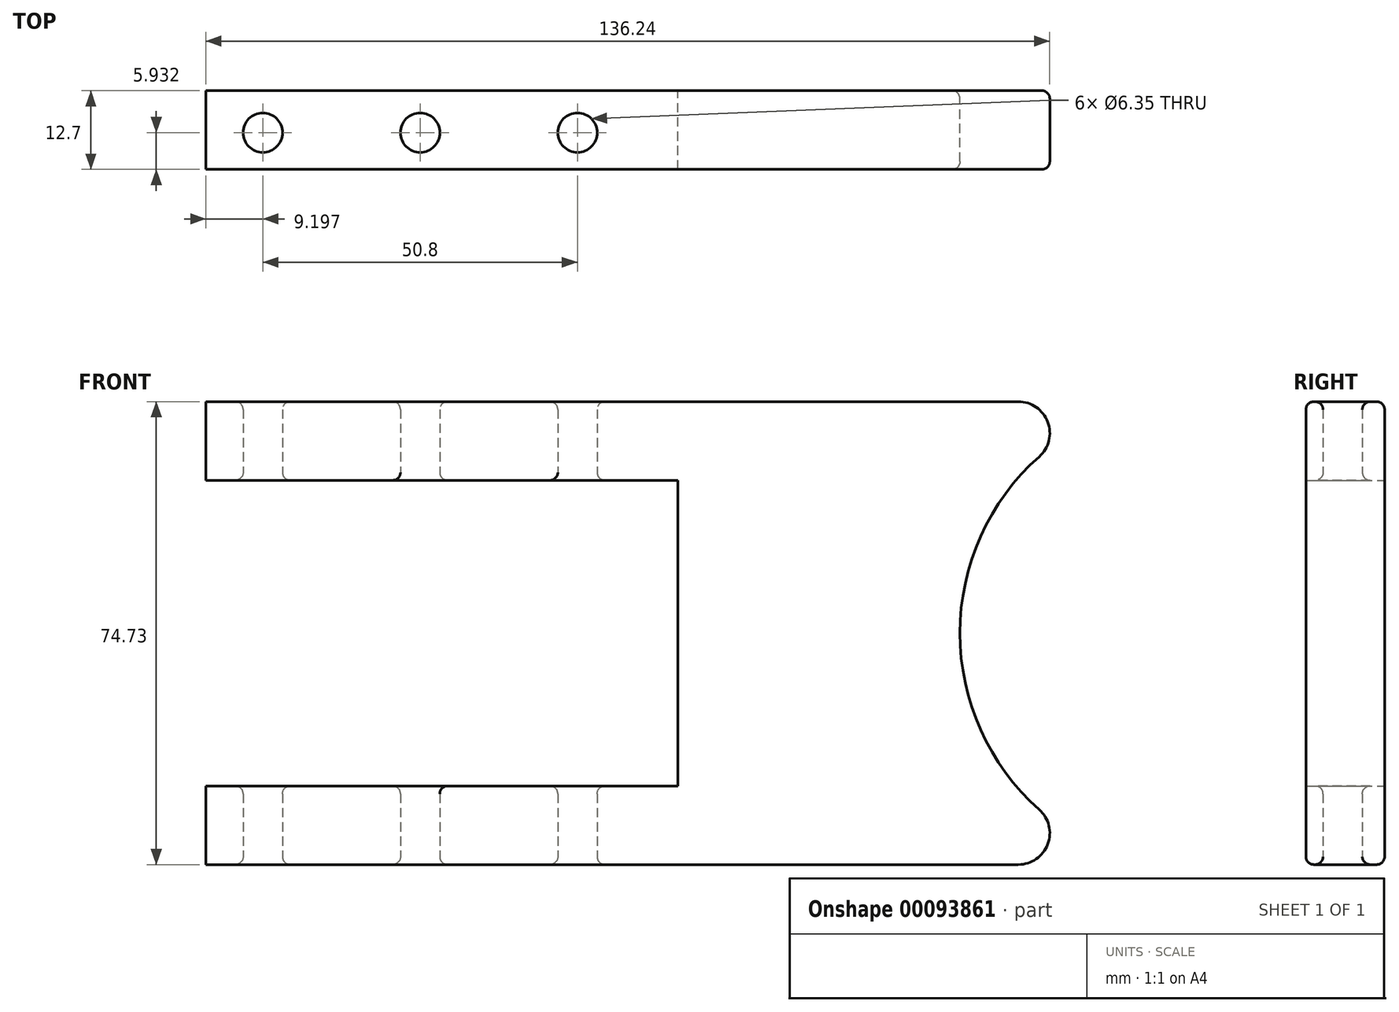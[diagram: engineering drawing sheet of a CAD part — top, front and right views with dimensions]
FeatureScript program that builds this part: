
annotation { "Feature Type Name" : "Feature", "Feature Type Description" : "" }
export const myFeature = defineFeature(function(context is Context, id is Id, definition is map)
    precondition{}
    {
        {
            var Q0;
            Q0=qCreatedBy(makeId("Front.planeOp"),FACE);
            var sketch = newSketch(context, id + "F0", { "sketchPlane" : qUnion([Q0])});
            skLineSegment(sketch, "E0.bottom", {"start": v(-76.46, 29.1) * mm, "end": v(75.94, 29.1) * mm});
            skLineSegment(sketch, "E0.top", {"start": v(-76.46, -45.63) * mm, "end": v(75.94, -45.63) * mm});
            skLineSegment(sketch, "E0.left", {"start": v(-76.46, 29.1) * mm, "end": v(-76.46, 16.4) * mm});
            skLineSegment(sketch, "E1", {"start": v(-76.46, 16.4) * mm, "end": v(-0.26, 16.4) * mm});
            skLineSegment(sketch, "E2", {"start": v(-0.26, 16.4) * mm, "end": v(-0.26, -32.93) * mm});
            skLineSegment(sketch, "E3", {"start": v(-0.26, -32.93) * mm, "end": v(-76.46, -32.93) * mm});
            skLineSegment(sketch, "E4.trimOffspring", {"start": v(-76.46, -32.93) * mm, "end": v(-76.46, -45.63) * mm});
            skArc(sketch, "E5", {"start": v(75.94, 29.1) * mm, "mid": v(45.28, -8.26) * mm, "end": v(75.94, -45.63) * mm});
            skSolve(sketch);
        }
        {
            var Q0;
            Q0=makeQuery(id+"F0.imprint","IMPRINT",FACE,{"disambiguationData":[TD([[makeQuery(id+"F0.imprint","IMPRINT",EDGE,{"derivedFrom":sQuery(id+"F0.wireOp",EDGE,"E0.bottom")}),-1.0]])]});
            extrude(context, id + "F1", {"entities" : qUnion([Q0]), "depth" : 12.7 * mm});
        }
        {
            var Q0;
            Q0=makeQuery(id+"F1.opExtrude","CAP_EDGE",EDGE,{"disambiguationData":[OSD([sQuery(id+"F0.wireOp",EDGE,"E0.bottom")])],"isStart":true});
            var Q1;
            Q1=makeQuery(id+"F1.opExtrude","CAP_EDGE",EDGE,{"disambiguationData":[OSD([sQuery(id+"F0.wireOp",EDGE,"E0.bottom")])],"isStart":false});
            var Q2;
            Q2=makeQuery(id+"F1.opExtrude","CAP_EDGE",EDGE,{"disambiguationData":[OSD([sQuery(id+"F0.wireOp",EDGE,"E5")])],"isStart":false});
            var Q3;
            Q3=makeQuery(id+"F1.opExtrude","CAP_EDGE",EDGE,{"disambiguationData":[OSD([sQuery(id+"F0.wireOp",EDGE,"E5")])],"isStart":true});
            var Q4;
            Q4=makeQuery(id+"F1.opExtrude","CAP_EDGE",EDGE,{"disambiguationData":[OSD([sQuery(id+"F0.wireOp",EDGE,"E0.top")])],"isStart":false});
            var Q5;
            Q5=makeQuery(id+"F1.opExtrude","CAP_EDGE",EDGE,{"disambiguationData":[OSD([sQuery(id+"F0.wireOp",EDGE,"E0.top")])],"isStart":true});
            fillet(context, id + "F2", {"entities" : qUnion([Q0, Q1, Q2, Q3, Q4, Q5]), "radius" : 1.27 * mm, "tangentPropagation" : true, "allowEdgeOverflow" : false});
        }
        {
            var Q0;
            Q0=qCreatedBy(makeId("Top.planeOp"),FACE);
            var sketch = newSketch(context, id + "F3", { "sketchPlane" : qUnion([Q0])});
            skCircle(sketch, "E6", {"center": v(-67.26, -6.77) * mm, "radius": 3.18 * mm});
            skCircle(sketch, "E7", {"center": v(-41.86, -6.77) * mm, "radius": 3.18 * mm});
            skCircle(sketch, "E8", {"center": v(-16.46, -6.77) * mm, "radius": 3.18 * mm});
            skSolve(sketch);
        }
        {
            var Q0;
            Q0=makeQuery(id+"F1.opExtrude","SWEPT_EDGE",EDGE,{"disambiguationData":[OSD([sQuery(id+"F0.wireOp",EDGE,"E0.bottom"),sQuery(id+"F0.wireOp",EDGE,"E5")])]});
            var Q1;
            Q1=makeQuery(id+"F1.opExtrude","SWEPT_EDGE",EDGE,{"disambiguationData":[OSD([sQuery(id+"F0.wireOp",EDGE,"E0.top"),sQuery(id+"F0.wireOp",EDGE,"E5")])]});
            fillet(context, id + "F4", {"entities" : qUnion([Q0, Q1]), "radius" : 5.08 * mm, "tangentPropagation" : true, "allowEdgeOverflow" : false});
        }
        {
            var Q0;
            Q0=makeQuery(id+"F3.imprint","IMPRINT",FACE,{"disambiguationData":[TD([[makeQuery(id+"F3.imprint","IMPRINT",EDGE,{"derivedFrom":sQuery(id+"F3.wireOp",EDGE,"E7")}),1.0]])]});
            var Q1;
            Q1=makeQuery(id+"F3.imprint","IMPRINT",FACE,{"disambiguationData":[TD([[makeQuery(id+"F3.imprint","IMPRINT",EDGE,{"derivedFrom":sQuery(id+"F3.wireOp",EDGE,"E8")}),1.0]])]});
            var Q2;
            Q2=makeQuery(id+"F3.imprint","IMPRINT",FACE,{"disambiguationData":[TD([[makeQuery(id+"F3.imprint","IMPRINT",EDGE,{"derivedFrom":sQuery(id+"F3.wireOp",EDGE,"E6")}),1.0]])]});
            var Q3;
            Q3=sQuery(id+"F3.wireOp",EDGE,"E8");
            var Q4;
            Q4=sQuery(id+"F3.wireOp",EDGE,"E7");
            var Q5;
            Q5=sQuery(id+"F3.wireOp",EDGE,"E6");
            extrude(context, id + "F5", {"entities" : qUnion([Q0, Q1, Q2]), "operationType" : NewBodyOperationType.REMOVE, "surfaceEntities" : qUnion([Q3, Q4, Q5]), "endBound" : BoundingType.SYMMETRIC, "depth" : 101.6 * mm});
        }
        {
            var Q0;
            Q0=makeQuery(id+"F5.boolean.opBoolean","INTERSECT",EDGE,{"derivedFrom":[makeQuery(id+"F1.opExtrude","SWEPT_FACE",FACE,{"disambiguationData":[OSD([sQuery(id+"F0.wireOp",EDGE,"E0.top")])]}),makeQuery(id+"F5.opExtrude","SWEPT_FACE",FACE,{"disambiguationData":[OSD([sQuery(id+"F3.wireOp",EDGE,"E7")])]})]});
            var Q1;
            Q1=makeQuery(id+"F5.boolean.opBoolean","INTERSECT",EDGE,{"derivedFrom":[makeQuery(id+"F1.opExtrude","SWEPT_FACE",FACE,{"disambiguationData":[OSD([sQuery(id+"F0.wireOp",EDGE,"E1")])]}),makeQuery(id+"F5.opExtrude","SWEPT_FACE",FACE,{"disambiguationData":[OSD([sQuery(id+"F3.wireOp",EDGE,"E7")])]})]});
            var Q2;
            Q2=makeQuery(id+"F5.boolean.opBoolean","INTERSECT",EDGE,{"derivedFrom":[makeQuery(id+"F1.opExtrude","SWEPT_FACE",FACE,{"disambiguationData":[OSD([sQuery(id+"F0.wireOp",EDGE,"E3")])]}),makeQuery(id+"F5.opExtrude","SWEPT_FACE",FACE,{"disambiguationData":[OSD([sQuery(id+"F3.wireOp",EDGE,"E7")])]})]});
            var Q3;
            Q3=makeQuery(id+"F5.boolean.opBoolean","INTERSECT",EDGE,{"derivedFrom":[makeQuery(id+"F1.opExtrude","SWEPT_FACE",FACE,{"disambiguationData":[OSD([sQuery(id+"F0.wireOp",EDGE,"E0.bottom")])]}),makeQuery(id+"F5.opExtrude","SWEPT_FACE",FACE,{"disambiguationData":[OSD([sQuery(id+"F3.wireOp",EDGE,"E7")])]})]});
            var Q4;
            Q4=makeQuery(id+"F5.boolean.opBoolean","INTERSECT",EDGE,{"derivedFrom":[makeQuery(id+"F1.opExtrude","SWEPT_FACE",FACE,{"disambiguationData":[OSD([sQuery(id+"F0.wireOp",EDGE,"E0.bottom")])]}),makeQuery(id+"F5.opExtrude","SWEPT_FACE",FACE,{"disambiguationData":[OSD([sQuery(id+"F3.wireOp",EDGE,"E8")])]})]});
            var Q5;
            Q5=makeQuery(id+"F5.boolean.opBoolean","INTERSECT",EDGE,{"derivedFrom":[makeQuery(id+"F1.opExtrude","SWEPT_FACE",FACE,{"disambiguationData":[OSD([sQuery(id+"F0.wireOp",EDGE,"E0.bottom")])]}),makeQuery(id+"F5.opExtrude","SWEPT_FACE",FACE,{"disambiguationData":[OSD([sQuery(id+"F3.wireOp",EDGE,"E6")])]})]});
            var Q6;
            Q6=makeQuery(id+"F5.boolean.opBoolean","INTERSECT",EDGE,{"derivedFrom":[makeQuery(id+"F1.opExtrude","SWEPT_FACE",FACE,{"disambiguationData":[OSD([sQuery(id+"F0.wireOp",EDGE,"E3")])]}),makeQuery(id+"F5.opExtrude","SWEPT_FACE",FACE,{"disambiguationData":[OSD([sQuery(id+"F3.wireOp",EDGE,"E8")])]})]});
            var Q7;
            Q7=makeQuery(id+"F5.boolean.opBoolean","COPY",FACE,{"disambiguationData":[OD(1.0)],"derivedFrom":makeQuery(id+"F5.opExtrude","SWEPT_FACE",FACE,{"disambiguationData":[OSD([sQuery(id+"F3.wireOp",EDGE,"E6")])]})});
            var Q8;
            Q8=makeQuery(id+"F5.boolean.opBoolean","INTERSECT",EDGE,{"derivedFrom":[makeQuery(id+"F1.opExtrude","SWEPT_FACE",FACE,{"disambiguationData":[OSD([sQuery(id+"F0.wireOp",EDGE,"E1")])]}),makeQuery(id+"F5.opExtrude","SWEPT_FACE",FACE,{"disambiguationData":[OSD([sQuery(id+"F3.wireOp",EDGE,"E6")])]})]});
            var Q9;
            Q9=makeQuery(id+"F5.boolean.opBoolean","INTERSECT",EDGE,{"derivedFrom":[makeQuery(id+"F1.opExtrude","SWEPT_FACE",FACE,{"disambiguationData":[OSD([sQuery(id+"F0.wireOp",EDGE,"E1")])]}),makeQuery(id+"F5.opExtrude","SWEPT_FACE",FACE,{"disambiguationData":[OSD([sQuery(id+"F3.wireOp",EDGE,"E8")])]})]});
            var Q10;
            Q10=makeQuery(id+"F5.boolean.opBoolean","COPY",FACE,{"disambiguationData":[OD(1.0)],"derivedFrom":makeQuery(id+"F5.opExtrude","SWEPT_FACE",FACE,{"disambiguationData":[OSD([sQuery(id+"F3.wireOp",EDGE,"E8")])]})});
            fillet(context, id + "F6", {"entities" : qUnion([Q0, Q1, Q2, Q3, Q4, Q5, Q6, Q7, Q8, Q9, Q10]), "radius" : 1.27 * mm, "tangentPropagation" : true, "allowEdgeOverflow" : false});
        }
    });
